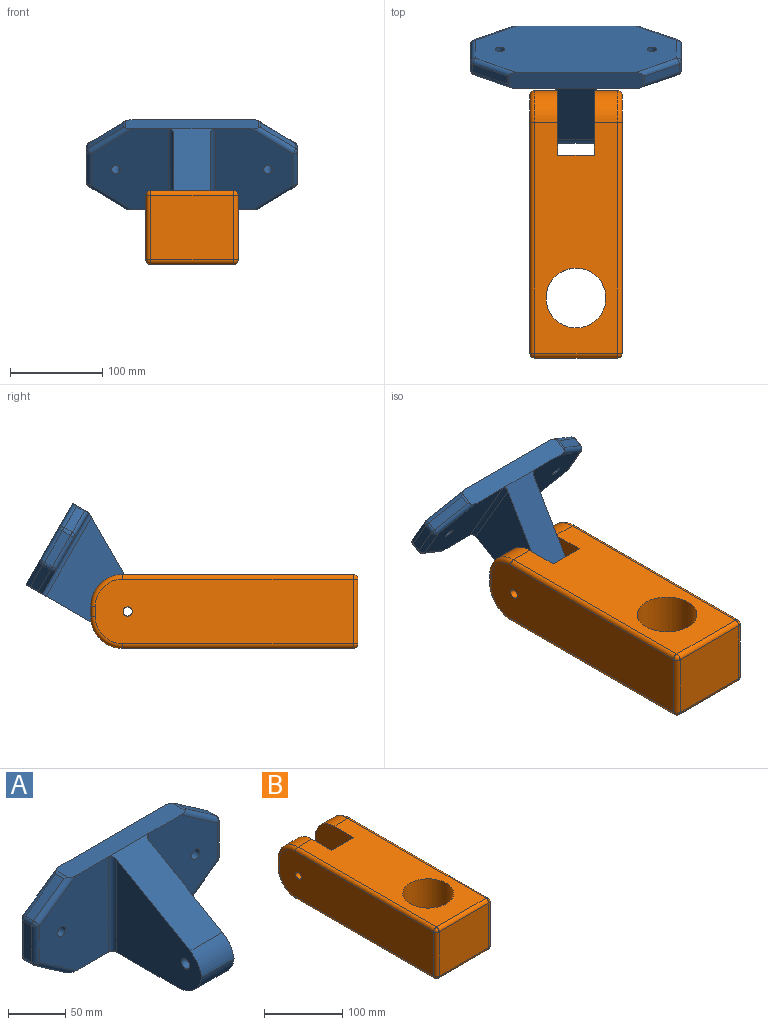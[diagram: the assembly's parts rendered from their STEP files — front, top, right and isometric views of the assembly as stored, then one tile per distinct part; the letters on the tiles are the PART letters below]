
ASSEMBLY  parts=2 mates=1
PART A: 49 faces, bbox 228.6x129.7x109.8 mm
  f0: plane 101.6x84.3mm, normal (0,-1,0), area 7088.8mm2, adj f3,f4,f11,f20,f37,f44,f45
  f1: plane 39.04x10mm, normal (1,0,0), area 390.4mm2, adj f38,f42,f45,f48
  f2: plane 37.53x26.28mm, normal (0.57,0,0.82), area 458.2mm2, adj f35,f36,f37,f38
  f3: plane 143.53x20mm, normal (0,0,1), area 2852.5mm2, adj f0,f5,f6,f13,f21,f22,f24,f35
  f4: cylinder r=5mm len=20mm, axis (0,-1,0), area 628.3mm2, adj f0,f5
  f5: plane 218.6x101.6mm, normal (0,1,0), area 19257.7mm2, adj f3,f4,f9,f11,f24,f29,f34,f36
  f6: plane 101.6x84.3mm, normal (0,-1,0), area 7088.8mm2, adj f3,f9,f11,f19,f21,f26,f31
  f7: plane 39.04x10mm, normal (-1,0,0), area 390.4mm2, adj f25,f26,f29,f30
  f8: plane 37.53x26.28mm, normal (-0.57,0,0.82), area 458.2mm2, adj f21,f22,f24,f25
  f9: cylinder r=5mm len=20mm, axis (0,-1,0), area 628.3mm2, adj f5,f6
  f10: plane 37.53x26.28mm, normal (0.57,0,-0.82), area 458.2mm2, adj f40,f43,f44,f48
  f11: plane 143.53x101.03mm, normal (0,0,-1), area 6104.4mm2, adj f0,f5,f6,f15,f16,f17,f19,f20
  f12: plane 37.53x26.28mm, normal (-0.57,0,-0.82), area 458.2mm2, adj f30,f31,f33,f34
  f13: plane 95.51x55.15mm, normal (0,-0.5,0.87), area 4424mm2, adj f3,f15,f16,f18,f19,f20
  f14: cylinder r=5mm len=40mm, axis (-1,0,0), area 1256.6mm2, adj f15,f16
  f15: plane 104.75x98.71mm, normal (1,0,0), area 6879.1mm2, adj f11,f13,f14,f17,f18,f20
  f16: plane 104.75x98.71mm, normal (-1,0,0), area 6879.1mm2, adj f11,f13,f14,f17,f18,f19
  f17: cylinder r=28.97mm len=40mm, axis (1,0,0), area 1667.7mm2, adj f11,f15,f16,f18
  f18: cylinder r=28.97mm len=40mm, axis (-1,0,0), area 1061mm2, adj f13,f15,f16,f17
  f19: cylinder r=5mm len=101.6mm, axis (0,0,-1), area 789.7mm2, adj f6,f11,f13,f16
  f20: cylinder r=5mm len=101.6mm, axis (0,0,1), area 789.7mm2, adj f0,f11,f13,f15
  f21: cylinder r=5mm len=47.54mm, axis (0.82,0,0.57), area 391mm2, adj f3,f6,f8,f22,f23
  f22: cylinder r=5mm len=15.74mm, axis (0,-1,0), area 39.6mm2, adj f3,f8,f21,f24
  f23: sphere r=5mm, area 24mm2, adj f21,f25,f26
  f24: cylinder r=5mm len=47.54mm, axis (-0.82,0,-0.57), area 391mm2, adj f3,f5,f8,f22,f27
  f25: cylinder r=5mm len=10mm, axis (0,-1,0), area 48mm2, adj f7,f8,f23,f27
  f26: cylinder r=5mm len=39.04mm, axis (0,0,1), area 306.6mm2, adj f6,f7,f23,f28
  f27: sphere r=5mm, area 24mm2, adj f24,f25,f29
  f28: sphere r=5mm, area 24mm2, adj f26,f30,f31
  f29: cylinder r=5mm len=39.04mm, axis (0,0,-1), area 306.6mm2, adj f5,f7,f27,f32
  f30: cylinder r=5mm len=10mm, axis (0,-1,0), area 48mm2, adj f7,f12,f28,f32
  f31: cylinder r=5mm len=47.54mm, axis (0.82,0,-0.57), area 391mm2, adj f6,f11,f12,f28,f33
  f32: sphere r=5mm, area 24mm2, adj f29,f30,f34
  f33: cylinder r=5mm len=15.74mm, axis (0,-1,0), area 39.6mm2, adj f11,f12,f31,f34
  f34: cylinder r=5mm len=47.54mm, axis (-0.82,0,0.57), area 391mm2, adj f5,f11,f12,f32,f33
  f35: cylinder r=5mm len=15.74mm, axis (0,-1,0), area 39.6mm2, adj f2,f3,f36,f37
  f36: cylinder r=5mm len=47.54mm, axis (0.82,0,-0.57), area 391mm2, adj f2,f3,f5,f35,f39
  f37: cylinder r=5mm len=47.54mm, axis (-0.82,0,0.57), area 391mm2, adj f0,f2,f3,f35,f41
  f38: cylinder r=5mm len=10mm, axis (0,-1,0), area 48mm2, adj f1,f2,f39,f41
  f39: sphere r=5mm, area 24mm2, adj f36,f38,f42
  f40: cylinder r=5mm len=15.74mm, axis (0,-1,0), area 39.6mm2, adj f10,f11,f43,f44
  f41: sphere r=5mm, area 24mm2, adj f37,f38,f45
  f42: cylinder r=5mm len=39.04mm, axis (0,0,-1), area 306.6mm2, adj f1,f5,f39,f46
  f43: cylinder r=5mm len=47.54mm, axis (0.82,0,0.57), area 391mm2, adj f5,f10,f11,f40,f46
  f44: cylinder r=5mm len=47.54mm, axis (-0.82,0,-0.57), area 391mm2, adj f0,f10,f11,f40,f47
  f45: cylinder r=5mm len=39.04mm, axis (0,0,1), area 306.6mm2, adj f0,f1,f41,f47
  f46: sphere r=5mm, area 24mm2, adj f42,f43,f48
  f47: sphere r=5mm, area 24mm2, adj f44,f45,f48
  f48: cylinder r=5mm len=10mm, axis (0,-1,0), area 48mm2, adj f1,f10,f46,f47
PART B: 35 faces, bbox 100x292.8x85.6 mm
  f0: plane 25x11.44mm, normal (0,1,0), area 285.9mm2, adj f1,f12,f14,f31
  f1: plane 80x70mm, normal (-1,0,0), area 5017mm2, adj f0,f2,f9,f10,f12,f14,f33
  f2: plane 80x40mm, normal (0,1,0), area 3200mm2, adj f1,f3,f9,f10
  f3: plane 80x70mm, normal (1,0,0), area 5017mm2, adj f2,f4,f9,f10,f11,f13,f34
  f4: plane 25x11.44mm, normal (0,1,0), area 285.9mm2, adj f3,f11,f13,f16
  f5: plane 280x70mm, normal (-1,0,0), area 19153.4mm2, adj f15,f16,f17,f18,f20,f21,f34
  f6: plane 90x70mm, normal (0,-1,0), area 6300mm2, adj f21,f22,f25,f26
  f7: plane 280x70mm, normal (1,0,0), area 19153.4mm2, adj f26,f27,f29,f30,f31,f32,f33
  f8: cylinder r=32.5mm len=80mm, axis (0,0,-1), area 16336.3mm2, adj f9,f10
  f9: plane 250.72x90mm, normal (0,0,1), area 17817.6mm2, adj f1,f2,f3,f8,f13,f14,f17,f22
  f10: plane 250.72x90mm, normal (0,0,-1), area 17817.6mm2, adj f1,f2,f3,f8,f11,f12,f20,f25
  f11: cylinder r=34.28mm len=34.28mm, axis (-1,0,0), area 1346.2mm2, adj f3,f4,f10,f18
  f12: cylinder r=34.28mm len=34.28mm, axis (-1,0,0), area 1346.2mm2, adj f0,f1,f10,f32
  f13: cylinder r=34.28mm len=34.28mm, axis (1,0,0), area 1346.2mm2, adj f3,f4,f9,f15
  f14: cylinder r=34.28mm len=34.28mm, axis (1,0,0), area 1346.2mm2, adj f0,f1,f9,f29
  f15: torus R=29.28mm, axis (-1,0,0), area 400.5mm2, adj f5,f13,f16,f17
  f16: cylinder r=5mm len=11.44mm, axis (0,0,-1), area 89.8mm2, adj f4,f5,f15,f18
  f17: cylinder r=5mm len=250.72mm, axis (0,1,0), area 1969.1mm2, adj f5,f9,f15,f19
  f18: torus R=29.28mm, axis (-1,0,0), area 400.5mm2, adj f5,f11,f16,f20
  f19: sphere r=5mm, area 39.3mm2, adj f17,f21,f22
  f20: cylinder r=5mm len=250.72mm, axis (0,-1,0), area 1969.1mm2, adj f5,f10,f18,f23
  f21: cylinder r=5mm len=70mm, axis (0,0,-1), area 549.8mm2, adj f5,f6,f19,f23
  f22: cylinder r=5mm len=90mm, axis (-1,0,0), area 706.9mm2, adj f6,f9,f19,f24
  f23: sphere r=5mm, area 39.3mm2, adj f20,f21,f25
  f24: sphere r=5mm, area 39.3mm2, adj f22,f26,f27
  f25: cylinder r=5mm len=90mm, axis (1,0,0), area 706.9mm2, adj f6,f10,f23,f28
  f26: cylinder r=5mm len=70mm, axis (0,0,-1), area 549.8mm2, adj f6,f7,f24,f28
  f27: cylinder r=5mm len=250.72mm, axis (0,-1,0), area 1969.1mm2, adj f7,f9,f24,f29
  f28: sphere r=5mm, area 39.3mm2, adj f25,f26,f30
  f29: torus R=29.28mm, axis (1,0,0), area 400.5mm2, adj f7,f14,f27,f31
  f30: cylinder r=5mm len=250.72mm, axis (0,1,0), area 1969.1mm2, adj f7,f10,f28,f32
  f31: cylinder r=5mm len=11.44mm, axis (0,0,-1), area 89.8mm2, adj f0,f7,f29,f32
  f32: torus R=29.28mm, axis (1,0,0), area 400.5mm2, adj f7,f12,f30,f31
  f33: cylinder r=5mm len=30mm, axis (-1,0,0), area 942.5mm2, adj f1,f7
  f34: cylinder r=5mm len=30mm, axis (-1,0,0), area 942.5mm2, adj f3,f5
PLACE A rot(axis=(1,0,0),30deg) t=(0,-116.26,-10.18)mm
PLACE B t=(-50,-433.8,-113.19)mm
MATE revolute B.f33 <-> A.f14  axis (-1,0,0) through (20,-183.8,-73.19)mm
